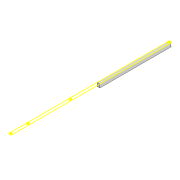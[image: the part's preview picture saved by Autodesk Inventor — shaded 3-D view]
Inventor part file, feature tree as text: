
AUTODESK INVENTOR PART (.ipt)
format: ipt  version: 2022 (Build 260153000, 153)  size: 104,960 bytes
history: native  units: mm
features: sketch x3, extrude x2, projected_geometry x1
ambient origin geometry x8: Origin, YZ Plane, XZ Plane, XY Plane, X Axis, Y Axis, Z Axis, Center Point
bodies: Solid1 (feature_tree)
feature tree (6):
  extrude  "Extrusion1"  Depth=6.0mm
  sketch  "Sketch2"  dims[d2=3.0mm d3=3.0mm]
  extrude  "Extrusion2"  Depth=3.0mm
  sketch  "Sketch1"  dims[d0=347.765mm d1=6.0mm]
  projected_geometry  "Projected Loop1"
  sketch  "Sketch3"  dims[d4=8.0mm d5=0.0mm d6=3.0mm d7=131.233mm d8=3.0mm d9=37.934mm d10=10.0mm d11=0.0mm]
